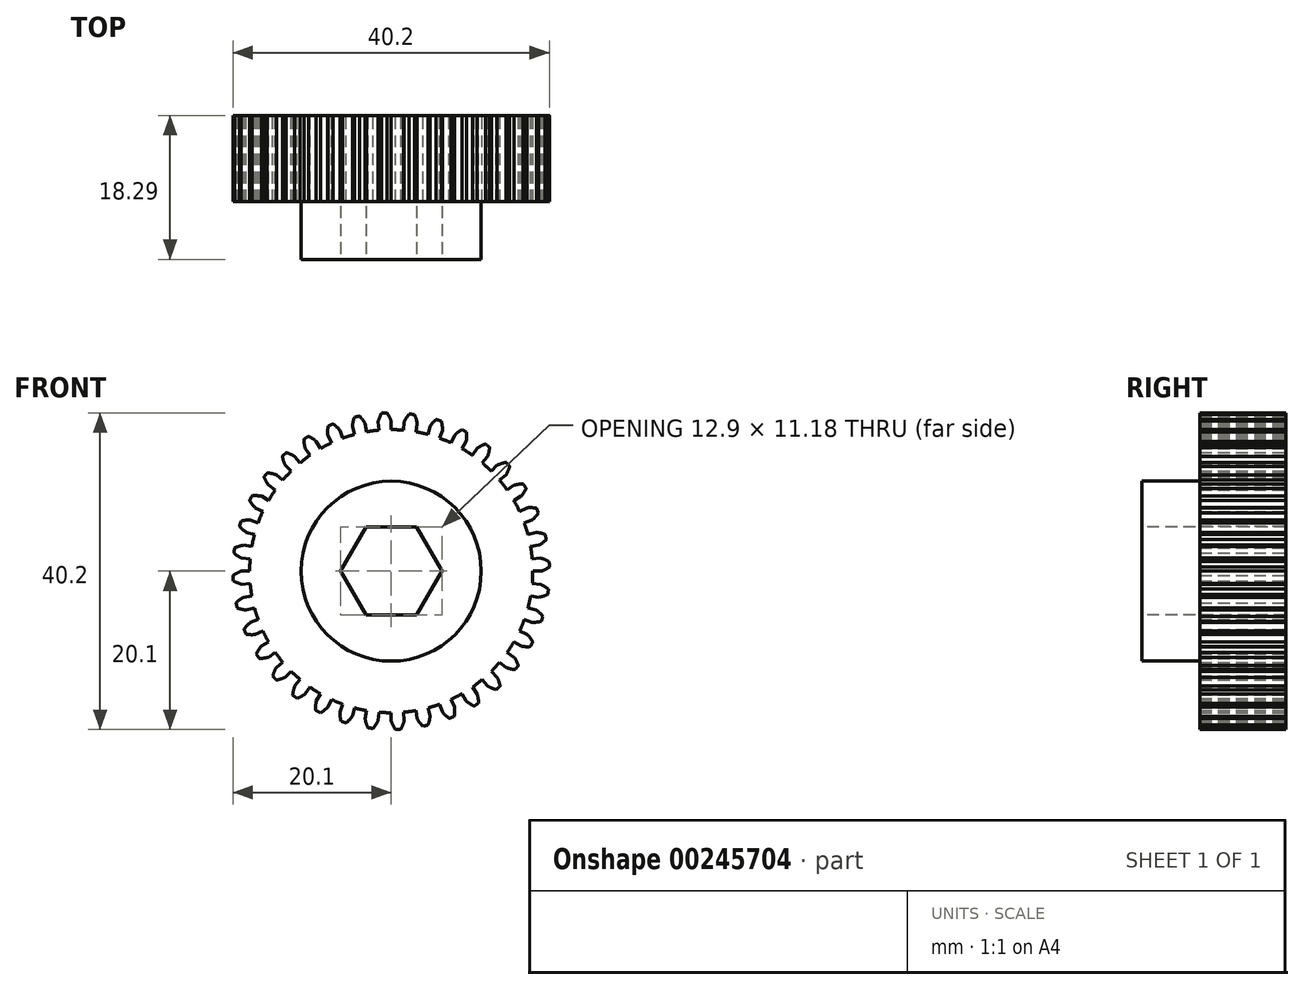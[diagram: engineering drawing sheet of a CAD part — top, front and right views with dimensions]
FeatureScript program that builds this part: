
annotation { "Feature Type Name" : "Feature", "Feature Type Description" : "" }
export const myFeature = defineFeature(function(context is Context, id is Id, definition is map)
    precondition{}
    {
        {
            var Q0;
            Q0=qCreatedBy(makeId("Front.planeOp"),FACE);
            var sketch = newSketch(context, id + "F0", { "sketchPlane" : qUnion([Q0])});
            skArc(sketch, "E0", {"start": v(-1.57, 17.91) * mm, "mid": v(-2.35, 17.83) * mm, "end": v(-3.12, 17.7) * mm});
            skLineSegment(sketch, "E1", {"start": v(0, 17.98) * mm, "end": v(0, 19.05) * mm});
            skPoint(sketch, "E2.orphan", {"position": v(-1, 22.9) * mm});
            skArc(sketch, "E3.trimOffspring", {"start": v(-0.54, 20.1) * mm, "mid": v(-0.7, 20.1) * mm, "end": v(-0.88, 20.08) * mm});
            skArc(sketch, "E4.trimOffspring", {"start": v(0, 19.05) * mm, "mid": v(-0.24, 19.6) * mm, "end": v(-0.54, 20.1) * mm});
            skPoint(sketch, "E5.trimOffspring.end.orphan", {"position": v(-2, 22.9) * mm});
            skArc(sketch, "E6.MirrorCS", {"start": v(-1.66, 18.98) * mm, "mid": v(-1.47, 19.54) * mm, "end": v(-1.22, 20.07) * mm});
            skArc(sketch, "E7.MirrorCS", {"start": v(-1.22, 20.07) * mm, "mid": v(-1.05, 20.08) * mm, "end": v(-0.88, 20.08) * mm});
            skLineSegment(sketch, "E8.MirrorCS", {"start": v(-1.57, 17.91) * mm, "end": v(-1.66, 18.98) * mm});
            skPoint(sketch, "E9.orphan", {"position": v(-2.73, 31.16) * mm});
            skPoint(sketch, "E10.orphan", {"position": v(0, 31.27) * mm});
            skLineSegment(sketch, "E11.1.0", {"start": v(-3.12, 17.7) * mm, "end": v(-3.3, 18.76) * mm});
            skArc(sketch, "E11.1.1", {"start": v(-3.3, 18.76) * mm, "mid": v(-3.63, 19.25) * mm, "end": v(-4.02, 19.7) * mm});
            skArc(sketch, "E11.1.2", {"start": v(-4.93, 18.4) * mm, "mid": v(-4.84, 18.98) * mm, "end": v(-4.68, 19.55) * mm});
            skLineSegment(sketch, "E11.1.3", {"start": v(-4.65, 17.37) * mm, "end": v(-4.93, 18.4) * mm});
            skArc(sketch, "E11.1.4", {"start": v(-4.68, 19.55) * mm, "mid": v(-4.52, 19.59) * mm, "end": v(-4.35, 19.63) * mm});
            skArc(sketch, "E11.1.5", {"start": v(-4.02, 19.7) * mm, "mid": v(-4.18, 19.66) * mm, "end": v(-4.35, 19.63) * mm});
            skLineSegment(sketch, "E11.2.0", {"start": v(-6.15, 16.9) * mm, "end": v(-6.52, 17.9) * mm});
            skArc(sketch, "E11.2.1", {"start": v(-6.52, 17.9) * mm, "mid": v(-6.92, 18.33) * mm, "end": v(-7.38, 18.7) * mm});
            skArc(sketch, "E11.2.2", {"start": v(-8.05, 17.27) * mm, "mid": v(-8.07, 17.85) * mm, "end": v(-8, 18.44) * mm});
            skLineSegment(sketch, "E11.2.3", {"start": v(-7.6, 16.3) * mm, "end": v(-8.05, 17.27) * mm});
            skArc(sketch, "E11.2.4", {"start": v(-8, 18.44) * mm, "mid": v(-7.85, 18.5) * mm, "end": v(-7.7, 18.57) * mm});
            skArc(sketch, "E11.2.5", {"start": v(-7.38, 18.7) * mm, "mid": v(-7.54, 18.64) * mm, "end": v(-7.7, 18.57) * mm});
            skLineSegment(sketch, "E11.3.0", {"start": v(-9, 15.57) * mm, "end": v(-9.52, 16.5) * mm});
            skArc(sketch, "E11.3.1", {"start": v(-9.52, 16.5) * mm, "mid": v(-10, 16.85) * mm, "end": v(-10.51, 17.14) * mm});
            skArc(sketch, "E11.3.2", {"start": v(-10.93, 15.6) * mm, "mid": v(-11.04, 16.18) * mm, "end": v(-11.09, 16.77) * mm});
            skLineSegment(sketch, "E11.3.3", {"start": v(-10.31, 14.73) * mm, "end": v(-10.93, 15.6) * mm});
            skArc(sketch, "E11.3.4", {"start": v(-11.09, 16.77) * mm, "mid": v(-10.95, 16.86) * mm, "end": v(-10.8, 16.96) * mm});
            skArc(sketch, "E11.3.5", {"start": v(-10.51, 17.14) * mm, "mid": v(-10.66, 17.05) * mm, "end": v(-10.8, 16.96) * mm});
            skLineSegment(sketch, "E11.4.0", {"start": v(-11.56, 13.78) * mm, "end": v(-12.25, 14.6) * mm});
            skArc(sketch, "E11.4.1", {"start": v(-12.25, 14.6) * mm, "mid": v(-12.77, 14.86) * mm, "end": v(-13.33, 15.05) * mm});
            skArc(sketch, "E11.4.2", {"start": v(-13.47, 13.47) * mm, "mid": v(-13.69, 14.02) * mm, "end": v(-13.83, 14.59) * mm});
            skLineSegment(sketch, "E11.4.3", {"start": v(-12.72, 12.72) * mm, "end": v(-13.47, 13.47) * mm});
            skArc(sketch, "E11.4.4", {"start": v(-13.83, 14.59) * mm, "mid": v(-13.7, 14.7) * mm, "end": v(-13.58, 14.82) * mm});
            skArc(sketch, "E11.4.5", {"start": v(-13.33, 15.05) * mm, "mid": v(-13.46, 14.94) * mm, "end": v(-13.58, 14.82) * mm});
            skLineSegment(sketch, "E11.5.0", {"start": v(-13.78, 11.56) * mm, "end": v(-14.6, 12.25) * mm});
            skArc(sketch, "E11.5.1", {"start": v(-14.6, 12.25) * mm, "mid": v(-15.16, 12.41) * mm, "end": v(-15.74, 12.5) * mm});
            skArc(sketch, "E11.5.2", {"start": v(-15.6, 10.93) * mm, "mid": v(-15.91, 11.43) * mm, "end": v(-16.16, 11.97) * mm});
            skLineSegment(sketch, "E11.5.3", {"start": v(-14.73, 10.31) * mm, "end": v(-15.6, 10.93) * mm});
            skArc(sketch, "E11.5.4", {"start": v(-16.16, 11.97) * mm, "mid": v(-16.05, 12.1) * mm, "end": v(-15.95, 12.24) * mm});
            skArc(sketch, "E11.5.5", {"start": v(-15.74, 12.5) * mm, "mid": v(-15.85, 12.37) * mm, "end": v(-15.95, 12.24) * mm});
            skLineSegment(sketch, "E11.6.0", {"start": v(-15.57, 9) * mm, "end": v(-16.5, 9.53) * mm});
            skArc(sketch, "E11.6.1", {"start": v(-16.5, 9.53) * mm, "mid": v(-17.08, 9.6) * mm, "end": v(-17.67, 9.58) * mm});
            skArc(sketch, "E11.6.2", {"start": v(-17.27, 8.05) * mm, "mid": v(-17.66, 8.5) * mm, "end": v(-17.99, 8.98) * mm});
            skLineSegment(sketch, "E11.6.3", {"start": v(-16.3, 7.6) * mm, "end": v(-17.27, 8.05) * mm});
            skArc(sketch, "E11.6.4", {"start": v(-17.99, 8.98) * mm, "mid": v(-17.91, 9.13) * mm, "end": v(-17.83, 9.28) * mm});
            skArc(sketch, "E11.6.5", {"start": v(-17.67, 9.58) * mm, "mid": v(-17.75, 9.43) * mm, "end": v(-17.83, 9.28) * mm});
            skLineSegment(sketch, "E11.7.0", {"start": v(-16.9, 6.15) * mm, "end": v(-17.9, 6.52) * mm});
            skArc(sketch, "E11.7.1", {"start": v(-17.9, 6.52) * mm, "mid": v(-18.49, 6.48) * mm, "end": v(-19.07, 6.37) * mm});
            skArc(sketch, "E11.7.2", {"start": v(-18.4, 4.93) * mm, "mid": v(-18.86, 5.3) * mm, "end": v(-19.27, 5.72) * mm});
            skLineSegment(sketch, "E11.7.3", {"start": v(-17.37, 4.65) * mm, "end": v(-18.4, 4.93) * mm});
            skArc(sketch, "E11.7.4", {"start": v(-19.27, 5.72) * mm, "mid": v(-19.22, 5.88) * mm, "end": v(-19.17, 6.05) * mm});
            skArc(sketch, "E11.7.5", {"start": v(-19.07, 6.37) * mm, "mid": v(-19.12, 6.2) * mm, "end": v(-19.17, 6.05) * mm});
            skLineSegment(sketch, "E11.8.0", {"start": v(-17.7, 3.12) * mm, "end": v(-18.76, 3.3) * mm});
            skArc(sketch, "E11.8.1", {"start": v(-18.76, 3.3) * mm, "mid": v(-19.33, 3.17) * mm, "end": v(-19.88, 2.96) * mm});
            skArc(sketch, "E11.8.2", {"start": v(-18.98, 1.66) * mm, "mid": v(-19.5, 1.94) * mm, "end": v(-19.97, 2.29) * mm});
            skLineSegment(sketch, "E11.8.3", {"start": v(-17.91, 1.57) * mm, "end": v(-18.98, 1.66) * mm});
            skArc(sketch, "E11.8.4", {"start": v(-19.97, 2.29) * mm, "mid": v(-19.95, 2.45) * mm, "end": v(-19.93, 2.62) * mm});
            skArc(sketch, "E11.8.5", {"start": v(-19.88, 2.96) * mm, "mid": v(-19.9, 2.8) * mm, "end": v(-19.93, 2.62) * mm});
            skLineSegment(sketch, "E11.9.0", {"start": v(-17.98, 0) * mm, "end": v(-19.05, 0) * mm});
            skArc(sketch, "E11.9.1", {"start": v(-19.05, 0) * mm, "mid": v(-19.6, -0.24) * mm, "end": v(-20.1, -0.54) * mm});
            skArc(sketch, "E11.9.2", {"start": v(-18.98, -1.66) * mm, "mid": v(-19.54, -1.47) * mm, "end": v(-20.07, -1.22) * mm});
            skLineSegment(sketch, "E11.9.3", {"start": v(-17.91, -1.57) * mm, "end": v(-18.98, -1.66) * mm});
            skArc(sketch, "E11.9.4", {"start": v(-20.07, -1.22) * mm, "mid": v(-20.08, -1.05) * mm, "end": v(-20.08, -0.88) * mm});
            skArc(sketch, "E11.9.5", {"start": v(-20.1, -0.54) * mm, "mid": v(-20.1, -0.7) * mm, "end": v(-20.08, -0.88) * mm});
            skLineSegment(sketch, "E11.10.0", {"start": v(-17.7, -3.12) * mm, "end": v(-18.76, -3.3) * mm});
            skArc(sketch, "E11.10.1", {"start": v(-18.76, -3.3) * mm, "mid": v(-19.25, -3.63) * mm, "end": v(-19.7, -4.02) * mm});
            skArc(sketch, "E11.10.2", {"start": v(-18.4, -4.93) * mm, "mid": v(-18.98, -4.84) * mm, "end": v(-19.55, -4.68) * mm});
            skLineSegment(sketch, "E11.10.3", {"start": v(-17.37, -4.65) * mm, "end": v(-18.4, -4.93) * mm});
            skArc(sketch, "E11.10.4", {"start": v(-19.55, -4.68) * mm, "mid": v(-19.59, -4.52) * mm, "end": v(-19.63, -4.35) * mm});
            skArc(sketch, "E11.10.5", {"start": v(-19.7, -4.02) * mm, "mid": v(-19.66, -4.18) * mm, "end": v(-19.63, -4.35) * mm});
            skLineSegment(sketch, "E11.11.0", {"start": v(-16.9, -6.15) * mm, "end": v(-17.9, -6.52) * mm});
            skArc(sketch, "E11.11.1", {"start": v(-17.9, -6.52) * mm, "mid": v(-18.33, -6.92) * mm, "end": v(-18.7, -7.38) * mm});
            skArc(sketch, "E11.11.2", {"start": v(-17.27, -8.05) * mm, "mid": v(-17.85, -8.07) * mm, "end": v(-18.44, -8) * mm});
            skLineSegment(sketch, "E11.11.3", {"start": v(-16.3, -7.6) * mm, "end": v(-17.27, -8.05) * mm});
            skArc(sketch, "E11.11.4", {"start": v(-18.44, -8) * mm, "mid": v(-18.5, -7.85) * mm, "end": v(-18.57, -7.7) * mm});
            skArc(sketch, "E11.11.5", {"start": v(-18.7, -7.38) * mm, "mid": v(-18.64, -7.54) * mm, "end": v(-18.57, -7.7) * mm});
            skLineSegment(sketch, "E11.12.0", {"start": v(-15.57, -9) * mm, "end": v(-16.5, -9.52) * mm});
            skArc(sketch, "E11.12.1", {"start": v(-16.5, -9.52) * mm, "mid": v(-16.85, -10) * mm, "end": v(-17.14, -10.51) * mm});
            skArc(sketch, "E11.12.2", {"start": v(-15.6, -10.93) * mm, "mid": v(-16.18, -11.04) * mm, "end": v(-16.77, -11.09) * mm});
            skLineSegment(sketch, "E11.12.3", {"start": v(-14.73, -10.31) * mm, "end": v(-15.6, -10.93) * mm});
            skArc(sketch, "E11.12.4", {"start": v(-16.77, -11.09) * mm, "mid": v(-16.86, -10.95) * mm, "end": v(-16.96, -10.8) * mm});
            skArc(sketch, "E11.12.5", {"start": v(-17.14, -10.51) * mm, "mid": v(-17.05, -10.66) * mm, "end": v(-16.96, -10.8) * mm});
            skLineSegment(sketch, "E11.13.0", {"start": v(-13.78, -11.56) * mm, "end": v(-14.6, -12.25) * mm});
            skArc(sketch, "E11.13.1", {"start": v(-14.6, -12.25) * mm, "mid": v(-14.86, -12.77) * mm, "end": v(-15.05, -13.33) * mm});
            skArc(sketch, "E11.13.2", {"start": v(-13.47, -13.47) * mm, "mid": v(-14.02, -13.69) * mm, "end": v(-14.59, -13.83) * mm});
            skLineSegment(sketch, "E11.13.3", {"start": v(-12.72, -12.72) * mm, "end": v(-13.47, -13.47) * mm});
            skArc(sketch, "E11.13.4", {"start": v(-14.59, -13.83) * mm, "mid": v(-14.7, -13.7) * mm, "end": v(-14.82, -13.58) * mm});
            skArc(sketch, "E11.13.5", {"start": v(-15.05, -13.33) * mm, "mid": v(-14.94, -13.46) * mm, "end": v(-14.82, -13.58) * mm});
            skLineSegment(sketch, "E11.14.0", {"start": v(-11.56, -13.78) * mm, "end": v(-12.25, -14.6) * mm});
            skArc(sketch, "E11.14.1", {"start": v(-12.25, -14.6) * mm, "mid": v(-12.41, -15.16) * mm, "end": v(-12.5, -15.74) * mm});
            skArc(sketch, "E11.14.2", {"start": v(-10.93, -15.6) * mm, "mid": v(-11.43, -15.91) * mm, "end": v(-11.97, -16.16) * mm});
            skLineSegment(sketch, "E11.14.3", {"start": v(-10.31, -14.73) * mm, "end": v(-10.93, -15.6) * mm});
            skArc(sketch, "E11.14.4", {"start": v(-11.97, -16.16) * mm, "mid": v(-12.1, -16.05) * mm, "end": v(-12.24, -15.95) * mm});
            skArc(sketch, "E11.14.5", {"start": v(-12.5, -15.74) * mm, "mid": v(-12.37, -15.85) * mm, "end": v(-12.24, -15.95) * mm});
            skLineSegment(sketch, "E11.15.0", {"start": v(-9, -15.57) * mm, "end": v(-9.53, -16.5) * mm});
            skArc(sketch, "E11.15.1", {"start": v(-9.53, -16.5) * mm, "mid": v(-9.6, -17.08) * mm, "end": v(-9.58, -17.67) * mm});
            skArc(sketch, "E11.15.2", {"start": v(-8.05, -17.27) * mm, "mid": v(-8.5, -17.66) * mm, "end": v(-8.98, -17.99) * mm});
            skLineSegment(sketch, "E11.15.3", {"start": v(-7.6, -16.3) * mm, "end": v(-8.05, -17.27) * mm});
            skArc(sketch, "E11.15.4", {"start": v(-8.98, -17.99) * mm, "mid": v(-9.13, -17.91) * mm, "end": v(-9.28, -17.83) * mm});
            skArc(sketch, "E11.15.5", {"start": v(-9.58, -17.67) * mm, "mid": v(-9.43, -17.75) * mm, "end": v(-9.28, -17.83) * mm});
            skLineSegment(sketch, "E11.16.0", {"start": v(-6.15, -16.9) * mm, "end": v(-6.52, -17.9) * mm});
            skArc(sketch, "E11.16.1", {"start": v(-6.52, -17.9) * mm, "mid": v(-6.48, -18.49) * mm, "end": v(-6.37, -19.07) * mm});
            skArc(sketch, "E11.16.2", {"start": v(-4.93, -18.4) * mm, "mid": v(-5.3, -18.86) * mm, "end": v(-5.72, -19.27) * mm});
            skLineSegment(sketch, "E11.16.3", {"start": v(-4.65, -17.37) * mm, "end": v(-4.93, -18.4) * mm});
            skArc(sketch, "E11.16.4", {"start": v(-5.72, -19.27) * mm, "mid": v(-5.88, -19.22) * mm, "end": v(-6.05, -19.17) * mm});
            skArc(sketch, "E11.16.5", {"start": v(-6.37, -19.07) * mm, "mid": v(-6.2, -19.12) * mm, "end": v(-6.05, -19.17) * mm});
            skLineSegment(sketch, "E11.17.0", {"start": v(-3.12, -17.7) * mm, "end": v(-3.3, -18.76) * mm});
            skArc(sketch, "E11.17.1", {"start": v(-3.3, -18.76) * mm, "mid": v(-3.17, -19.33) * mm, "end": v(-2.96, -19.88) * mm});
            skArc(sketch, "E11.17.2", {"start": v(-1.66, -18.98) * mm, "mid": v(-1.94, -19.5) * mm, "end": v(-2.29, -19.97) * mm});
            skLineSegment(sketch, "E11.17.3", {"start": v(-1.57, -17.91) * mm, "end": v(-1.66, -18.98) * mm});
            skArc(sketch, "E11.17.4", {"start": v(-2.29, -19.97) * mm, "mid": v(-2.45, -19.95) * mm, "end": v(-2.62, -19.93) * mm});
            skArc(sketch, "E11.17.5", {"start": v(-2.96, -19.88) * mm, "mid": v(-2.8, -19.9) * mm, "end": v(-2.62, -19.93) * mm});
            skLineSegment(sketch, "E11.18.0", {"start": v(0, -17.98) * mm, "end": v(0, -19.05) * mm});
            skArc(sketch, "E11.18.1", {"start": v(0, -19.05) * mm, "mid": v(0.24, -19.6) * mm, "end": v(0.54, -20.1) * mm});
            skArc(sketch, "E11.18.2", {"start": v(1.66, -18.98) * mm, "mid": v(1.47, -19.54) * mm, "end": v(1.22, -20.07) * mm});
            skLineSegment(sketch, "E11.18.3", {"start": v(1.57, -17.91) * mm, "end": v(1.66, -18.98) * mm});
            skArc(sketch, "E11.18.4", {"start": v(1.22, -20.07) * mm, "mid": v(1.05, -20.08) * mm, "end": v(0.88, -20.08) * mm});
            skArc(sketch, "E11.18.5", {"start": v(0.54, -20.1) * mm, "mid": v(0.7, -20.1) * mm, "end": v(0.88, -20.08) * mm});
            skLineSegment(sketch, "E11.19.0", {"start": v(3.12, -17.7) * mm, "end": v(3.3, -18.76) * mm});
            skArc(sketch, "E11.19.1", {"start": v(3.3, -18.76) * mm, "mid": v(3.63, -19.25) * mm, "end": v(4.02, -19.7) * mm});
            skArc(sketch, "E11.19.2", {"start": v(4.93, -18.4) * mm, "mid": v(4.84, -18.98) * mm, "end": v(4.68, -19.55) * mm});
            skLineSegment(sketch, "E11.19.3", {"start": v(4.65, -17.37) * mm, "end": v(4.93, -18.4) * mm});
            skArc(sketch, "E11.19.4", {"start": v(4.68, -19.55) * mm, "mid": v(4.52, -19.59) * mm, "end": v(4.35, -19.63) * mm});
            skArc(sketch, "E11.19.5", {"start": v(4.02, -19.7) * mm, "mid": v(4.18, -19.66) * mm, "end": v(4.35, -19.63) * mm});
            skLineSegment(sketch, "E11.20.0", {"start": v(6.15, -16.9) * mm, "end": v(6.52, -17.9) * mm});
            skArc(sketch, "E11.20.1", {"start": v(6.52, -17.9) * mm, "mid": v(6.92, -18.33) * mm, "end": v(7.38, -18.7) * mm});
            skArc(sketch, "E11.20.2", {"start": v(8.05, -17.27) * mm, "mid": v(8.07, -17.85) * mm, "end": v(8, -18.44) * mm});
            skLineSegment(sketch, "E11.20.3", {"start": v(7.6, -16.3) * mm, "end": v(8.05, -17.27) * mm});
            skArc(sketch, "E11.20.4", {"start": v(8, -18.44) * mm, "mid": v(7.85, -18.5) * mm, "end": v(7.7, -18.57) * mm});
            skArc(sketch, "E11.20.5", {"start": v(7.38, -18.7) * mm, "mid": v(7.54, -18.64) * mm, "end": v(7.7, -18.57) * mm});
            skLineSegment(sketch, "E11.21.0", {"start": v(9, -15.57) * mm, "end": v(9.53, -16.5) * mm});
            skArc(sketch, "E11.21.1", {"start": v(9.53, -16.5) * mm, "mid": v(10, -16.85) * mm, "end": v(10.51, -17.14) * mm});
            skArc(sketch, "E11.21.2", {"start": v(10.93, -15.6) * mm, "mid": v(11.04, -16.18) * mm, "end": v(11.09, -16.77) * mm});
            skLineSegment(sketch, "E11.21.3", {"start": v(10.31, -14.73) * mm, "end": v(10.93, -15.6) * mm});
            skArc(sketch, "E11.21.4", {"start": v(11.09, -16.77) * mm, "mid": v(10.95, -16.86) * mm, "end": v(10.8, -16.96) * mm});
            skArc(sketch, "E11.21.5", {"start": v(10.51, -17.14) * mm, "mid": v(10.66, -17.05) * mm, "end": v(10.8, -16.96) * mm});
            skLineSegment(sketch, "E11.22.0", {"start": v(11.56, -13.78) * mm, "end": v(12.25, -14.6) * mm});
            skArc(sketch, "E11.22.1", {"start": v(12.25, -14.6) * mm, "mid": v(12.77, -14.86) * mm, "end": v(13.33, -15.05) * mm});
            skArc(sketch, "E11.22.2", {"start": v(13.47, -13.47) * mm, "mid": v(13.69, -14.02) * mm, "end": v(13.83, -14.59) * mm});
            skLineSegment(sketch, "E11.22.3", {"start": v(12.72, -12.72) * mm, "end": v(13.47, -13.47) * mm});
            skArc(sketch, "E11.22.4", {"start": v(13.83, -14.59) * mm, "mid": v(13.7, -14.7) * mm, "end": v(13.58, -14.82) * mm});
            skArc(sketch, "E11.22.5", {"start": v(13.33, -15.05) * mm, "mid": v(13.46, -14.94) * mm, "end": v(13.58, -14.82) * mm});
            skLineSegment(sketch, "E11.23.0", {"start": v(13.78, -11.56) * mm, "end": v(14.6, -12.25) * mm});
            skArc(sketch, "E11.23.1", {"start": v(14.6, -12.25) * mm, "mid": v(15.16, -12.41) * mm, "end": v(15.74, -12.5) * mm});
            skArc(sketch, "E11.23.2", {"start": v(15.6, -10.93) * mm, "mid": v(15.91, -11.43) * mm, "end": v(16.16, -11.97) * mm});
            skLineSegment(sketch, "E11.23.3", {"start": v(14.73, -10.31) * mm, "end": v(15.6, -10.93) * mm});
            skArc(sketch, "E11.23.4", {"start": v(16.16, -11.97) * mm, "mid": v(16.05, -12.1) * mm, "end": v(15.95, -12.24) * mm});
            skArc(sketch, "E11.23.5", {"start": v(15.74, -12.5) * mm, "mid": v(15.85, -12.37) * mm, "end": v(15.95, -12.24) * mm});
            skLineSegment(sketch, "E11.24.0", {"start": v(15.57, -9) * mm, "end": v(16.5, -9.53) * mm});
            skArc(sketch, "E11.24.1", {"start": v(16.5, -9.53) * mm, "mid": v(17.08, -9.6) * mm, "end": v(17.67, -9.58) * mm});
            skArc(sketch, "E11.24.2", {"start": v(17.27, -8.05) * mm, "mid": v(17.66, -8.5) * mm, "end": v(17.99, -8.98) * mm});
            skLineSegment(sketch, "E11.24.3", {"start": v(16.3, -7.6) * mm, "end": v(17.27, -8.05) * mm});
            skArc(sketch, "E11.24.4", {"start": v(17.99, -8.98) * mm, "mid": v(17.91, -9.13) * mm, "end": v(17.83, -9.28) * mm});
            skArc(sketch, "E11.24.5", {"start": v(17.67, -9.58) * mm, "mid": v(17.75, -9.43) * mm, "end": v(17.83, -9.28) * mm});
            skLineSegment(sketch, "E11.25.0", {"start": v(16.9, -6.15) * mm, "end": v(17.9, -6.52) * mm});
            skArc(sketch, "E11.25.1", {"start": v(17.9, -6.52) * mm, "mid": v(18.49, -6.48) * mm, "end": v(19.07, -6.37) * mm});
            skArc(sketch, "E11.25.2", {"start": v(18.4, -4.93) * mm, "mid": v(18.86, -5.3) * mm, "end": v(19.27, -5.72) * mm});
            skLineSegment(sketch, "E11.25.3", {"start": v(17.37, -4.65) * mm, "end": v(18.4, -4.93) * mm});
            skArc(sketch, "E11.25.4", {"start": v(19.27, -5.72) * mm, "mid": v(19.22, -5.88) * mm, "end": v(19.17, -6.05) * mm});
            skArc(sketch, "E11.25.5", {"start": v(19.07, -6.37) * mm, "mid": v(19.12, -6.2) * mm, "end": v(19.17, -6.05) * mm});
            skLineSegment(sketch, "E11.26.0", {"start": v(17.7, -3.12) * mm, "end": v(18.76, -3.3) * mm});
            skArc(sketch, "E11.26.1", {"start": v(18.76, -3.3) * mm, "mid": v(19.33, -3.17) * mm, "end": v(19.88, -2.96) * mm});
            skArc(sketch, "E11.26.2", {"start": v(18.98, -1.66) * mm, "mid": v(19.5, -1.94) * mm, "end": v(19.97, -2.29) * mm});
            skLineSegment(sketch, "E11.26.3", {"start": v(17.91, -1.57) * mm, "end": v(18.98, -1.66) * mm});
            skArc(sketch, "E11.26.4", {"start": v(19.97, -2.29) * mm, "mid": v(19.95, -2.45) * mm, "end": v(19.93, -2.62) * mm});
            skArc(sketch, "E11.26.5", {"start": v(19.88, -2.96) * mm, "mid": v(19.9, -2.8) * mm, "end": v(19.93, -2.62) * mm});
            skLineSegment(sketch, "E11.27.0", {"start": v(17.98, 0) * mm, "end": v(19.05, 0) * mm});
            skArc(sketch, "E11.27.1", {"start": v(19.05, 0) * mm, "mid": v(19.6, 0.24) * mm, "end": v(20.1, 0.54) * mm});
            skArc(sketch, "E11.27.2", {"start": v(18.98, 1.66) * mm, "mid": v(19.54, 1.47) * mm, "end": v(20.07, 1.22) * mm});
            skLineSegment(sketch, "E11.27.3", {"start": v(17.91, 1.57) * mm, "end": v(18.98, 1.66) * mm});
            skArc(sketch, "E11.27.4", {"start": v(20.07, 1.22) * mm, "mid": v(20.08, 1.05) * mm, "end": v(20.08, 0.88) * mm});
            skArc(sketch, "E11.27.5", {"start": v(20.1, 0.54) * mm, "mid": v(20.1, 0.7) * mm, "end": v(20.08, 0.88) * mm});
            skLineSegment(sketch, "E11.28.0", {"start": v(17.7, 3.12) * mm, "end": v(18.76, 3.3) * mm});
            skArc(sketch, "E11.28.1", {"start": v(18.76, 3.3) * mm, "mid": v(19.25, 3.63) * mm, "end": v(19.7, 4.02) * mm});
            skArc(sketch, "E11.28.2", {"start": v(18.4, 4.93) * mm, "mid": v(18.98, 4.84) * mm, "end": v(19.55, 4.68) * mm});
            skLineSegment(sketch, "E11.28.3", {"start": v(17.37, 4.65) * mm, "end": v(18.4, 4.93) * mm});
            skArc(sketch, "E11.28.4", {"start": v(19.55, 4.68) * mm, "mid": v(19.59, 4.52) * mm, "end": v(19.63, 4.35) * mm});
            skArc(sketch, "E11.28.5", {"start": v(19.7, 4.02) * mm, "mid": v(19.66, 4.18) * mm, "end": v(19.63, 4.35) * mm});
            skLineSegment(sketch, "E11.29.0", {"start": v(16.9, 6.15) * mm, "end": v(17.9, 6.52) * mm});
            skArc(sketch, "E11.29.1", {"start": v(17.9, 6.52) * mm, "mid": v(18.33, 6.92) * mm, "end": v(18.7, 7.38) * mm});
            skArc(sketch, "E11.29.2", {"start": v(17.27, 8.05) * mm, "mid": v(17.85, 8.07) * mm, "end": v(18.44, 8) * mm});
            skLineSegment(sketch, "E11.29.3", {"start": v(16.3, 7.6) * mm, "end": v(17.27, 8.05) * mm});
            skArc(sketch, "E11.29.4", {"start": v(18.44, 8) * mm, "mid": v(18.5, 7.85) * mm, "end": v(18.57, 7.7) * mm});
            skArc(sketch, "E11.29.5", {"start": v(18.7, 7.38) * mm, "mid": v(18.64, 7.54) * mm, "end": v(18.57, 7.7) * mm});
            skLineSegment(sketch, "E11.30.0", {"start": v(15.57, 9) * mm, "end": v(16.5, 9.52) * mm});
            skArc(sketch, "E11.30.1", {"start": v(16.5, 9.52) * mm, "mid": v(16.85, 10) * mm, "end": v(17.14, 10.51) * mm});
            skArc(sketch, "E11.30.2", {"start": v(15.6, 10.93) * mm, "mid": v(16.18, 11.04) * mm, "end": v(16.77, 11.09) * mm});
            skLineSegment(sketch, "E11.30.3", {"start": v(14.73, 10.31) * mm, "end": v(15.6, 10.93) * mm});
            skArc(sketch, "E11.30.4", {"start": v(16.77, 11.09) * mm, "mid": v(16.86, 10.95) * mm, "end": v(16.96, 10.8) * mm});
            skArc(sketch, "E11.30.5", {"start": v(17.14, 10.51) * mm, "mid": v(17.05, 10.66) * mm, "end": v(16.96, 10.8) * mm});
            skLineSegment(sketch, "E11.31.0", {"start": v(13.78, 11.56) * mm, "end": v(14.6, 12.25) * mm});
            skArc(sketch, "E11.31.1", {"start": v(14.6, 12.25) * mm, "mid": v(14.86, 12.77) * mm, "end": v(15.05, 13.33) * mm});
            skArc(sketch, "E11.31.2", {"start": v(13.47, 13.47) * mm, "mid": v(14.02, 13.69) * mm, "end": v(14.59, 13.83) * mm});
            skLineSegment(sketch, "E11.31.3", {"start": v(12.72, 12.72) * mm, "end": v(13.47, 13.47) * mm});
            skArc(sketch, "E11.31.4", {"start": v(14.59, 13.83) * mm, "mid": v(14.7, 13.7) * mm, "end": v(14.82, 13.58) * mm});
            skArc(sketch, "E11.31.5", {"start": v(15.05, 13.33) * mm, "mid": v(14.94, 13.46) * mm, "end": v(14.82, 13.58) * mm});
            skLineSegment(sketch, "E11.32.0", {"start": v(11.56, 13.78) * mm, "end": v(12.25, 14.6) * mm});
            skArc(sketch, "E11.32.1", {"start": v(12.25, 14.6) * mm, "mid": v(12.41, 15.16) * mm, "end": v(12.5, 15.74) * mm});
            skArc(sketch, "E11.32.2", {"start": v(10.93, 15.6) * mm, "mid": v(11.43, 15.91) * mm, "end": v(11.97, 16.16) * mm});
            skLineSegment(sketch, "E11.32.3", {"start": v(10.31, 14.73) * mm, "end": v(10.93, 15.6) * mm});
            skArc(sketch, "E11.32.4", {"start": v(11.97, 16.16) * mm, "mid": v(12.1, 16.05) * mm, "end": v(12.24, 15.95) * mm});
            skArc(sketch, "E11.32.5", {"start": v(12.5, 15.74) * mm, "mid": v(12.37, 15.85) * mm, "end": v(12.24, 15.95) * mm});
            skLineSegment(sketch, "E11.33.0", {"start": v(9, 15.57) * mm, "end": v(9.52, 16.5) * mm});
            skArc(sketch, "E11.33.1", {"start": v(9.52, 16.5) * mm, "mid": v(9.6, 17.08) * mm, "end": v(9.58, 17.67) * mm});
            skArc(sketch, "E11.33.2", {"start": v(8.05, 17.27) * mm, "mid": v(8.5, 17.66) * mm, "end": v(8.98, 17.99) * mm});
            skLineSegment(sketch, "E11.33.3", {"start": v(7.6, 16.3) * mm, "end": v(8.05, 17.27) * mm});
            skArc(sketch, "E11.33.4", {"start": v(8.98, 17.99) * mm, "mid": v(9.13, 17.91) * mm, "end": v(9.28, 17.83) * mm});
            skArc(sketch, "E11.33.5", {"start": v(9.58, 17.67) * mm, "mid": v(9.43, 17.75) * mm, "end": v(9.28, 17.83) * mm});
            skLineSegment(sketch, "E11.34.0", {"start": v(6.15, 16.9) * mm, "end": v(6.52, 17.9) * mm});
            skArc(sketch, "E11.34.1", {"start": v(6.52, 17.9) * mm, "mid": v(6.48, 18.49) * mm, "end": v(6.37, 19.07) * mm});
            skArc(sketch, "E11.34.2", {"start": v(4.93, 18.4) * mm, "mid": v(5.3, 18.86) * mm, "end": v(5.72, 19.27) * mm});
            skLineSegment(sketch, "E11.34.3", {"start": v(4.65, 17.37) * mm, "end": v(4.93, 18.4) * mm});
            skArc(sketch, "E11.34.4", {"start": v(5.72, 19.27) * mm, "mid": v(5.88, 19.22) * mm, "end": v(6.05, 19.17) * mm});
            skArc(sketch, "E11.34.5", {"start": v(6.37, 19.07) * mm, "mid": v(6.2, 19.12) * mm, "end": v(6.05, 19.17) * mm});
            skLineSegment(sketch, "E11.35.0", {"start": v(3.12, 17.7) * mm, "end": v(3.3, 18.76) * mm});
            skArc(sketch, "E11.35.1", {"start": v(3.3, 18.76) * mm, "mid": v(3.17, 19.33) * mm, "end": v(2.96, 19.88) * mm});
            skArc(sketch, "E11.35.2", {"start": v(1.66, 18.98) * mm, "mid": v(1.94, 19.5) * mm, "end": v(2.29, 19.97) * mm});
            skLineSegment(sketch, "E11.35.3", {"start": v(1.57, 17.91) * mm, "end": v(1.66, 18.98) * mm});
            skArc(sketch, "E11.35.4", {"start": v(2.29, 19.97) * mm, "mid": v(2.45, 19.95) * mm, "end": v(2.62, 19.93) * mm});
            skArc(sketch, "E11.35.5", {"start": v(2.96, 19.88) * mm, "mid": v(2.8, 19.9) * mm, "end": v(2.62, 19.93) * mm});
            skArc(sketch, "E12.trimOffspring", {"start": v(-4.65, 17.37) * mm, "mid": v(-5.4, 17.15) * mm, "end": v(-6.15, 16.9) * mm});
            skArc(sketch, "E13.trimOffspring", {"start": v(-7.6, 16.3) * mm, "mid": v(-8.3, 15.95) * mm, "end": v(-9, 15.57) * mm});
            skArc(sketch, "E14.trimOffspring", {"start": v(-10.31, 14.73) * mm, "mid": v(-10.95, 14.27) * mm, "end": v(-11.56, 13.78) * mm});
            skArc(sketch, "E15.trimOffspring", {"start": v(-12.72, 12.72) * mm, "mid": v(-13.26, 12.15) * mm, "end": v(-13.78, 11.56) * mm});
            skArc(sketch, "E16.trimOffspring", {"start": v(-14.73, 10.31) * mm, "mid": v(-15.17, 9.66) * mm, "end": v(-15.57, 9) * mm});
            skArc(sketch, "E17.trimOffspring", {"start": v(-16.3, 7.6) * mm, "mid": v(-16.61, 6.88) * mm, "end": v(-16.9, 6.15) * mm});
            skArc(sketch, "E18.trimOffspring", {"start": v(-17.37, 4.65) * mm, "mid": v(-17.56, 3.9) * mm, "end": v(-17.7, 3.12) * mm});
            skArc(sketch, "E19.trimOffspring", {"start": v(-17.91, 1.57) * mm, "mid": v(-17.97, 0.78) * mm, "end": v(-17.98, 0) * mm});
            skArc(sketch, "E20.trimOffspring", {"start": v(-17.91, -1.57) * mm, "mid": v(-17.83, -2.35) * mm, "end": v(-17.7, -3.12) * mm});
            skArc(sketch, "E21.trimOffspring", {"start": v(-17.37, -4.65) * mm, "mid": v(-17.15, -5.4) * mm, "end": v(-16.9, -6.15) * mm});
            skArc(sketch, "E22.trimOffspring", {"start": v(-16.3, -7.6) * mm, "mid": v(-15.95, -8.3) * mm, "end": v(-15.57, -9) * mm});
            skArc(sketch, "E23.trimOffspring", {"start": v(1.57, 17.91) * mm, "mid": v(0.78, 17.97) * mm, "end": v(0, 17.98) * mm});
            skArc(sketch, "E24.trimOffspring", {"start": v(4.65, 17.37) * mm, "mid": v(3.9, 17.56) * mm, "end": v(3.12, 17.7) * mm});
            skArc(sketch, "E25.trimOffspring", {"start": v(7.6, 16.3) * mm, "mid": v(6.88, 16.61) * mm, "end": v(6.15, 16.9) * mm});
            skArc(sketch, "E26.trimOffspring", {"start": v(10.31, 14.73) * mm, "mid": v(9.66, 15.17) * mm, "end": v(9, 15.57) * mm});
            skArc(sketch, "E27.trimOffspring", {"start": v(12.72, 12.72) * mm, "mid": v(12.15, 13.26) * mm, "end": v(11.56, 13.78) * mm});
            skArc(sketch, "E28.trimOffspring", {"start": v(14.73, 10.31) * mm, "mid": v(14.27, 10.95) * mm, "end": v(13.78, 11.56) * mm});
            skArc(sketch, "E29.trimOffspring", {"start": v(16.3, 7.6) * mm, "mid": v(15.95, 8.3) * mm, "end": v(15.57, 9) * mm});
            skArc(sketch, "E30.trimOffspring", {"start": v(17.37, 4.65) * mm, "mid": v(17.15, 5.4) * mm, "end": v(16.9, 6.15) * mm});
            skArc(sketch, "E31.trimOffspring", {"start": v(17.91, 1.57) * mm, "mid": v(17.83, 2.35) * mm, "end": v(17.7, 3.12) * mm});
            skArc(sketch, "E32.trimOffspring", {"start": v(17.91, -1.57) * mm, "mid": v(17.97, -0.78) * mm, "end": v(17.98, 0) * mm});
            skArc(sketch, "E33.trimOffspring", {"start": v(17.37, -4.65) * mm, "mid": v(17.56, -3.9) * mm, "end": v(17.7, -3.12) * mm});
            skArc(sketch, "E34.trimOffspring", {"start": v(16.3, -7.6) * mm, "mid": v(16.61, -6.88) * mm, "end": v(16.9, -6.15) * mm});
            skArc(sketch, "E35.trimOffspring", {"start": v(14.73, -10.31) * mm, "mid": v(15.17, -9.66) * mm, "end": v(15.57, -9) * mm});
            skArc(sketch, "E36.trimOffspring", {"start": v(12.72, -12.72) * mm, "mid": v(13.26, -12.15) * mm, "end": v(13.78, -11.56) * mm});
            skArc(sketch, "E37.trimOffspring", {"start": v(10.31, -14.73) * mm, "mid": v(10.95, -14.27) * mm, "end": v(11.56, -13.78) * mm});
            skArc(sketch, "E38.trimOffspring", {"start": v(7.6, -16.3) * mm, "mid": v(8.3, -15.95) * mm, "end": v(9, -15.57) * mm});
            skArc(sketch, "E39.trimOffspring", {"start": v(4.65, -17.37) * mm, "mid": v(5.4, -17.15) * mm, "end": v(6.15, -16.9) * mm});
            skArc(sketch, "E40.trimOffspring", {"start": v(1.57, -17.91) * mm, "mid": v(2.35, -17.83) * mm, "end": v(3.12, -17.7) * mm});
            skArc(sketch, "E41.trimOffspring", {"start": v(-1.57, -17.91) * mm, "mid": v(-0.78, -17.97) * mm, "end": v(0, -17.98) * mm});
            skArc(sketch, "E42.trimOffspring", {"start": v(-4.65, -17.37) * mm, "mid": v(-3.9, -17.56) * mm, "end": v(-3.12, -17.7) * mm});
            skArc(sketch, "E43.trimOffspring", {"start": v(-7.6, -16.3) * mm, "mid": v(-6.88, -16.61) * mm, "end": v(-6.15, -16.9) * mm});
            skArc(sketch, "E44.trimOffspring", {"start": v(-10.31, -14.73) * mm, "mid": v(-9.66, -15.17) * mm, "end": v(-9, -15.57) * mm});
            skArc(sketch, "E45.trimOffspring", {"start": v(-12.72, -12.72) * mm, "mid": v(-12.15, -13.26) * mm, "end": v(-11.56, -13.78) * mm});
            skArc(sketch, "E46.trimOffspring", {"start": v(-14.73, -10.31) * mm, "mid": v(-14.27, -10.95) * mm, "end": v(-13.78, -11.56) * mm});
            skSolve(sketch);
        }
        {
            var Q0;
            Q0=makeQuery(id+"F0.imprint","IMPRINT",FACE,{"disambiguationData":[TD([[makeQuery(id+"F0.imprint","IMPRINT",EDGE,{"derivedFrom":sQuery(id+"F0.wireOp",EDGE,"E0")}),1.0]])]});
            extrude(context, id + "F1", {"entities" : qUnion([Q0]), "depth" : 10.92 * mm});
        }
        {
            var Q0;
            Q0=makeQuery(id+"F1.opExtrude","CAP_FACE",FACE,{"disambiguationData":[OSD([sQuery(id+"F0.wireOp",EDGE,"E0"),sQuery(id+"F0.wireOp",EDGE,"E1"),sQuery(id+"F0.wireOp",EDGE,"E3.trimOffspring"),sQuery(id+"F0.wireOp",EDGE,"E4.trimOffspring"),sQuery(id+"F0.wireOp",EDGE,"E6.MirrorCS"),sQuery(id+"F0.wireOp",EDGE,"E7.MirrorCS"),sQuery(id+"F0.wireOp",EDGE,"E8.MirrorCS"),sQuery(id+"F0.wireOp",EDGE,"E11.1.0"),sQuery(id+"F0.wireOp",EDGE,"E11.1.1"),sQuery(id+"F0.wireOp",EDGE,"E11.1.2"),sQuery(id+"F0.wireOp",EDGE,"E11.1.3"),sQuery(id+"F0.wireOp",EDGE,"E11.1.4"),sQuery(id+"F0.wireOp",EDGE,"E11.1.5"),sQuery(id+"F0.wireOp",EDGE,"E11.2.0"),sQuery(id+"F0.wireOp",EDGE,"E11.2.1"),sQuery(id+"F0.wireOp",EDGE,"E11.2.2"),sQuery(id+"F0.wireOp",EDGE,"E11.2.3"),sQuery(id+"F0.wireOp",EDGE,"E11.2.4"),sQuery(id+"F0.wireOp",EDGE,"E11.2.5"),sQuery(id+"F0.wireOp",EDGE,"E11.3.0"),sQuery(id+"F0.wireOp",EDGE,"E11.3.1"),sQuery(id+"F0.wireOp",EDGE,"E11.3.2"),sQuery(id+"F0.wireOp",EDGE,"E11.3.3"),sQuery(id+"F0.wireOp",EDGE,"E11.3.4"),sQuery(id+"F0.wireOp",EDGE,"E11.3.5"),sQuery(id+"F0.wireOp",EDGE,"E11.4.0"),sQuery(id+"F0.wireOp",EDGE,"E11.4.1"),sQuery(id+"F0.wireOp",EDGE,"E11.4.2"),sQuery(id+"F0.wireOp",EDGE,"E11.4.3"),sQuery(id+"F0.wireOp",EDGE,"E11.4.4"),sQuery(id+"F0.wireOp",EDGE,"E11.4.5"),sQuery(id+"F0.wireOp",EDGE,"E11.5.0"),sQuery(id+"F0.wireOp",EDGE,"E11.5.1"),sQuery(id+"F0.wireOp",EDGE,"E11.5.2"),sQuery(id+"F0.wireOp",EDGE,"E11.5.3"),sQuery(id+"F0.wireOp",EDGE,"E11.5.4"),sQuery(id+"F0.wireOp",EDGE,"E11.5.5"),sQuery(id+"F0.wireOp",EDGE,"E11.6.0"),sQuery(id+"F0.wireOp",EDGE,"E11.6.1"),sQuery(id+"F0.wireOp",EDGE,"E11.6.2"),sQuery(id+"F0.wireOp",EDGE,"E11.6.3"),sQuery(id+"F0.wireOp",EDGE,"E11.6.4"),sQuery(id+"F0.wireOp",EDGE,"E11.6.5"),sQuery(id+"F0.wireOp",EDGE,"E11.7.0"),sQuery(id+"F0.wireOp",EDGE,"E11.7.1"),sQuery(id+"F0.wireOp",EDGE,"E11.7.2"),sQuery(id+"F0.wireOp",EDGE,"E11.7.3"),sQuery(id+"F0.wireOp",EDGE,"E11.7.4"),sQuery(id+"F0.wireOp",EDGE,"E11.7.5"),sQuery(id+"F0.wireOp",EDGE,"E11.8.0"),sQuery(id+"F0.wireOp",EDGE,"E11.8.1"),sQuery(id+"F0.wireOp",EDGE,"E11.8.2"),sQuery(id+"F0.wireOp",EDGE,"E11.8.3"),sQuery(id+"F0.wireOp",EDGE,"E11.8.4"),sQuery(id+"F0.wireOp",EDGE,"E11.8.5"),sQuery(id+"F0.wireOp",EDGE,"E11.9.0"),sQuery(id+"F0.wireOp",EDGE,"E11.9.1"),sQuery(id+"F0.wireOp",EDGE,"E11.9.2"),sQuery(id+"F0.wireOp",EDGE,"E11.9.3"),sQuery(id+"F0.wireOp",EDGE,"E11.9.4"),sQuery(id+"F0.wireOp",EDGE,"E11.9.5"),sQuery(id+"F0.wireOp",EDGE,"E11.10.0"),sQuery(id+"F0.wireOp",EDGE,"E11.10.1"),sQuery(id+"F0.wireOp",EDGE,"E11.10.2"),sQuery(id+"F0.wireOp",EDGE,"E11.10.3"),sQuery(id+"F0.wireOp",EDGE,"E11.10.4"),sQuery(id+"F0.wireOp",EDGE,"E11.10.5"),sQuery(id+"F0.wireOp",EDGE,"E11.11.0"),sQuery(id+"F0.wireOp",EDGE,"E11.11.1"),sQuery(id+"F0.wireOp",EDGE,"E11.11.2"),sQuery(id+"F0.wireOp",EDGE,"E11.11.3"),sQuery(id+"F0.wireOp",EDGE,"E11.11.4"),sQuery(id+"F0.wireOp",EDGE,"E11.11.5"),sQuery(id+"F0.wireOp",EDGE,"E11.12.0"),sQuery(id+"F0.wireOp",EDGE,"E11.12.1"),sQuery(id+"F0.wireOp",EDGE,"E11.12.2"),sQuery(id+"F0.wireOp",EDGE,"E11.12.3"),sQuery(id+"F0.wireOp",EDGE,"E11.12.4"),sQuery(id+"F0.wireOp",EDGE,"E11.12.5"),sQuery(id+"F0.wireOp",EDGE,"E11.13.0"),sQuery(id+"F0.wireOp",EDGE,"E11.13.1"),sQuery(id+"F0.wireOp",EDGE,"E11.13.2"),sQuery(id+"F0.wireOp",EDGE,"E11.13.3"),sQuery(id+"F0.wireOp",EDGE,"E11.13.4"),sQuery(id+"F0.wireOp",EDGE,"E11.13.5"),sQuery(id+"F0.wireOp",EDGE,"E11.14.0"),sQuery(id+"F0.wireOp",EDGE,"E11.14.1"),sQuery(id+"F0.wireOp",EDGE,"E11.14.2"),sQuery(id+"F0.wireOp",EDGE,"E11.14.3"),sQuery(id+"F0.wireOp",EDGE,"E11.14.4"),sQuery(id+"F0.wireOp",EDGE,"E11.14.5"),sQuery(id+"F0.wireOp",EDGE,"E11.15.0"),sQuery(id+"F0.wireOp",EDGE,"E11.15.1"),sQuery(id+"F0.wireOp",EDGE,"E11.15.2"),sQuery(id+"F0.wireOp",EDGE,"E11.15.3"),sQuery(id+"F0.wireOp",EDGE,"E11.15.4"),sQuery(id+"F0.wireOp",EDGE,"E11.15.5"),sQuery(id+"F0.wireOp",EDGE,"E11.16.0"),sQuery(id+"F0.wireOp",EDGE,"E11.16.1"),sQuery(id+"F0.wireOp",EDGE,"E11.16.2"),sQuery(id+"F0.wireOp",EDGE,"E11.16.3"),sQuery(id+"F0.wireOp",EDGE,"E11.16.4"),sQuery(id+"F0.wireOp",EDGE,"E11.16.5"),sQuery(id+"F0.wireOp",EDGE,"E11.17.0"),sQuery(id+"F0.wireOp",EDGE,"E11.17.1"),sQuery(id+"F0.wireOp",EDGE,"E11.17.2"),sQuery(id+"F0.wireOp",EDGE,"E11.17.3"),sQuery(id+"F0.wireOp",EDGE,"E11.17.4"),sQuery(id+"F0.wireOp",EDGE,"E11.17.5"),sQuery(id+"F0.wireOp",EDGE,"E11.18.0"),sQuery(id+"F0.wireOp",EDGE,"E11.18.1"),sQuery(id+"F0.wireOp",EDGE,"E11.18.2"),sQuery(id+"F0.wireOp",EDGE,"E11.18.3"),sQuery(id+"F0.wireOp",EDGE,"E11.18.4"),sQuery(id+"F0.wireOp",EDGE,"E11.18.5"),sQuery(id+"F0.wireOp",EDGE,"E11.19.0"),sQuery(id+"F0.wireOp",EDGE,"E11.19.1"),sQuery(id+"F0.wireOp",EDGE,"E11.19.2"),sQuery(id+"F0.wireOp",EDGE,"E11.19.3"),sQuery(id+"F0.wireOp",EDGE,"E11.19.4"),sQuery(id+"F0.wireOp",EDGE,"E11.19.5"),sQuery(id+"F0.wireOp",EDGE,"E11.20.0"),sQuery(id+"F0.wireOp",EDGE,"E11.20.1"),sQuery(id+"F0.wireOp",EDGE,"E11.20.2"),sQuery(id+"F0.wireOp",EDGE,"E11.20.3"),sQuery(id+"F0.wireOp",EDGE,"E11.20.4"),sQuery(id+"F0.wireOp",EDGE,"E11.20.5"),sQuery(id+"F0.wireOp",EDGE,"E11.21.0"),sQuery(id+"F0.wireOp",EDGE,"E11.21.1"),sQuery(id+"F0.wireOp",EDGE,"E11.21.2"),sQuery(id+"F0.wireOp",EDGE,"E11.21.3"),sQuery(id+"F0.wireOp",EDGE,"E11.21.4"),sQuery(id+"F0.wireOp",EDGE,"E11.21.5"),sQuery(id+"F0.wireOp",EDGE,"E11.22.0"),sQuery(id+"F0.wireOp",EDGE,"E11.22.1"),sQuery(id+"F0.wireOp",EDGE,"E11.22.2"),sQuery(id+"F0.wireOp",EDGE,"E11.22.3"),sQuery(id+"F0.wireOp",EDGE,"E11.22.4"),sQuery(id+"F0.wireOp",EDGE,"E11.22.5"),sQuery(id+"F0.wireOp",EDGE,"E11.23.0"),sQuery(id+"F0.wireOp",EDGE,"E11.23.1"),sQuery(id+"F0.wireOp",EDGE,"E11.23.2"),sQuery(id+"F0.wireOp",EDGE,"E11.23.3"),sQuery(id+"F0.wireOp",EDGE,"E11.23.4"),sQuery(id+"F0.wireOp",EDGE,"E11.23.5"),sQuery(id+"F0.wireOp",EDGE,"E11.24.0"),sQuery(id+"F0.wireOp",EDGE,"E11.24.1"),sQuery(id+"F0.wireOp",EDGE,"E11.24.2"),sQuery(id+"F0.wireOp",EDGE,"E11.24.3"),sQuery(id+"F0.wireOp",EDGE,"E11.24.4"),sQuery(id+"F0.wireOp",EDGE,"E11.24.5"),sQuery(id+"F0.wireOp",EDGE,"E11.25.0"),sQuery(id+"F0.wireOp",EDGE,"E11.25.1"),sQuery(id+"F0.wireOp",EDGE,"E11.25.2"),sQuery(id+"F0.wireOp",EDGE,"E11.25.3"),sQuery(id+"F0.wireOp",EDGE,"E11.25.4"),sQuery(id+"F0.wireOp",EDGE,"E11.25.5"),sQuery(id+"F0.wireOp",EDGE,"E11.26.0"),sQuery(id+"F0.wireOp",EDGE,"E11.26.1"),sQuery(id+"F0.wireOp",EDGE,"E11.26.2"),sQuery(id+"F0.wireOp",EDGE,"E11.26.3"),sQuery(id+"F0.wireOp",EDGE,"E11.26.4"),sQuery(id+"F0.wireOp",EDGE,"E11.26.5"),sQuery(id+"F0.wireOp",EDGE,"E11.27.0"),sQuery(id+"F0.wireOp",EDGE,"E11.27.1"),sQuery(id+"F0.wireOp",EDGE,"E11.27.2"),sQuery(id+"F0.wireOp",EDGE,"E11.27.3"),sQuery(id+"F0.wireOp",EDGE,"E11.27.4"),sQuery(id+"F0.wireOp",EDGE,"E11.27.5"),sQuery(id+"F0.wireOp",EDGE,"E11.28.0"),sQuery(id+"F0.wireOp",EDGE,"E11.28.1"),sQuery(id+"F0.wireOp",EDGE,"E11.28.2"),sQuery(id+"F0.wireOp",EDGE,"E11.28.3"),sQuery(id+"F0.wireOp",EDGE,"E11.28.4"),sQuery(id+"F0.wireOp",EDGE,"E11.28.5"),sQuery(id+"F0.wireOp",EDGE,"E11.29.0"),sQuery(id+"F0.wireOp",EDGE,"E11.29.1"),sQuery(id+"F0.wireOp",EDGE,"E11.29.2"),sQuery(id+"F0.wireOp",EDGE,"E11.29.3"),sQuery(id+"F0.wireOp",EDGE,"E11.29.4"),sQuery(id+"F0.wireOp",EDGE,"E11.29.5"),sQuery(id+"F0.wireOp",EDGE,"E11.30.0"),sQuery(id+"F0.wireOp",EDGE,"E11.30.1"),sQuery(id+"F0.wireOp",EDGE,"E11.30.2"),sQuery(id+"F0.wireOp",EDGE,"E11.30.3"),sQuery(id+"F0.wireOp",EDGE,"E11.30.4"),sQuery(id+"F0.wireOp",EDGE,"E11.30.5"),sQuery(id+"F0.wireOp",EDGE,"E11.31.0"),sQuery(id+"F0.wireOp",EDGE,"E11.31.1"),sQuery(id+"F0.wireOp",EDGE,"E11.31.2"),sQuery(id+"F0.wireOp",EDGE,"E11.31.3"),sQuery(id+"F0.wireOp",EDGE,"E11.31.4"),sQuery(id+"F0.wireOp",EDGE,"E11.31.5"),sQuery(id+"F0.wireOp",EDGE,"E11.32.0"),sQuery(id+"F0.wireOp",EDGE,"E11.32.1"),sQuery(id+"F0.wireOp",EDGE,"E11.32.2"),sQuery(id+"F0.wireOp",EDGE,"E11.32.3"),sQuery(id+"F0.wireOp",EDGE,"E11.32.4"),sQuery(id+"F0.wireOp",EDGE,"E11.32.5"),sQuery(id+"F0.wireOp",EDGE,"E11.33.0"),sQuery(id+"F0.wireOp",EDGE,"E11.33.1"),sQuery(id+"F0.wireOp",EDGE,"E11.33.2"),sQuery(id+"F0.wireOp",EDGE,"E11.33.3"),sQuery(id+"F0.wireOp",EDGE,"E11.33.4"),sQuery(id+"F0.wireOp",EDGE,"E11.33.5"),sQuery(id+"F0.wireOp",EDGE,"E11.34.0"),sQuery(id+"F0.wireOp",EDGE,"E11.34.1"),sQuery(id+"F0.wireOp",EDGE,"E11.34.2"),sQuery(id+"F0.wireOp",EDGE,"E11.34.3"),sQuery(id+"F0.wireOp",EDGE,"E11.34.4"),sQuery(id+"F0.wireOp",EDGE,"E11.34.5"),sQuery(id+"F0.wireOp",EDGE,"E11.35.0"),sQuery(id+"F0.wireOp",EDGE,"E11.35.1"),sQuery(id+"F0.wireOp",EDGE,"E11.35.2"),sQuery(id+"F0.wireOp",EDGE,"E11.35.3"),sQuery(id+"F0.wireOp",EDGE,"E11.35.4"),sQuery(id+"F0.wireOp",EDGE,"E11.35.5"),sQuery(id+"F0.wireOp",EDGE,"E12.trimOffspring"),sQuery(id+"F0.wireOp",EDGE,"E13.trimOffspring"),sQuery(id+"F0.wireOp",EDGE,"E14.trimOffspring"),sQuery(id+"F0.wireOp",EDGE,"E15.trimOffspring"),sQuery(id+"F0.wireOp",EDGE,"E16.trimOffspring"),sQuery(id+"F0.wireOp",EDGE,"E17.trimOffspring"),sQuery(id+"F0.wireOp",EDGE,"E18.trimOffspring"),sQuery(id+"F0.wireOp",EDGE,"E19.trimOffspring"),sQuery(id+"F0.wireOp",EDGE,"E20.trimOffspring"),sQuery(id+"F0.wireOp",EDGE,"E21.trimOffspring"),sQuery(id+"F0.wireOp",EDGE,"E22.trimOffspring"),sQuery(id+"F0.wireOp",EDGE,"E23.trimOffspring"),sQuery(id+"F0.wireOp",EDGE,"E24.trimOffspring"),sQuery(id+"F0.wireOp",EDGE,"E25.trimOffspring"),sQuery(id+"F0.wireOp",EDGE,"E26.trimOffspring"),sQuery(id+"F0.wireOp",EDGE,"E27.trimOffspring"),sQuery(id+"F0.wireOp",EDGE,"E28.trimOffspring"),sQuery(id+"F0.wireOp",EDGE,"E29.trimOffspring"),sQuery(id+"F0.wireOp",EDGE,"E30.trimOffspring"),sQuery(id+"F0.wireOp",EDGE,"E31.trimOffspring"),sQuery(id+"F0.wireOp",EDGE,"E32.trimOffspring"),sQuery(id+"F0.wireOp",EDGE,"E33.trimOffspring"),sQuery(id+"F0.wireOp",EDGE,"E34.trimOffspring"),sQuery(id+"F0.wireOp",EDGE,"E35.trimOffspring"),sQuery(id+"F0.wireOp",EDGE,"E36.trimOffspring"),sQuery(id+"F0.wireOp",EDGE,"E37.trimOffspring"),sQuery(id+"F0.wireOp",EDGE,"E38.trimOffspring"),sQuery(id+"F0.wireOp",EDGE,"E39.trimOffspring"),sQuery(id+"F0.wireOp",EDGE,"E40.trimOffspring"),sQuery(id+"F0.wireOp",EDGE,"E41.trimOffspring"),sQuery(id+"F0.wireOp",EDGE,"E42.trimOffspring"),sQuery(id+"F0.wireOp",EDGE,"E43.trimOffspring"),sQuery(id+"F0.wireOp",EDGE,"E44.trimOffspring"),sQuery(id+"F0.wireOp",EDGE,"E45.trimOffspring"),sQuery(id+"F0.wireOp",EDGE,"E46.trimOffspring")])],"isStart":false});
            var sketch = newSketch(context, id + "F2", { "sketchPlane" : qUnion([Q0])});
            skCircle(sketch, "E47", {"center": v(0, 0) * mm, "radius": 11.43 * mm});
            skSolve(sketch);
        }
        {
            var Q0;
            Q0 = qSketchRegion(id + "F2", true);
            extrude(context, id + "F3", {"entities" : qUnion([Q0]), "operationType" : NewBodyOperationType.ADD, "depth" : 7.37 * mm});
        }
        {
            var Q0;
            Q0=makeQuery(id+"F3.opExtrude","CAP_FACE",FACE,{"disambiguationData":[OSD([sQuery(id+"F2.wireOp",EDGE,"E47")])],"isStart":false});
            var sketch = newSketch(context, id + "F4", { "sketchPlane" : qUnion([Q0])});
            skCircle(sketch, "E48.cCircle", {"center": v(0, 0) * mm, "radius": 5.59 * mm, "construction": true});
            skLineSegment(sketch, "E48.0", {"start": v(-3.23, 5.59) * mm, "end": v(3.23, 5.59) * mm});
            skLineSegment(sketch, "E48.1", {"start": v(3.23, 5.59) * mm, "end": v(6.45, 0) * mm});
            skLineSegment(sketch, "E48.2", {"start": v(6.45, 0) * mm, "end": v(3.23, -5.59) * mm});
            skLineSegment(sketch, "E48.3", {"start": v(3.23, -5.59) * mm, "end": v(-3.23, -5.59) * mm});
            skLineSegment(sketch, "E48.4", {"start": v(-3.23, -5.59) * mm, "end": v(-6.45, 0) * mm});
            skLineSegment(sketch, "E48.5", {"start": v(-6.45, 0) * mm, "end": v(-3.23, 5.59) * mm});
            skPoint(sketch, "E48.0.midPoint", {"position": v(0, 5.59) * mm});
            skSolve(sketch);
        }
        {
            var Q0;
            Q0 = qSketchRegion(id + "F4", true);
            extrude(context, id + "F5", {"entities" : qUnion([Q0]), "operationType" : NewBodyOperationType.REMOVE, "oppositeDirection" : true, "depth" : 92.2 * mm});
        }
    });
